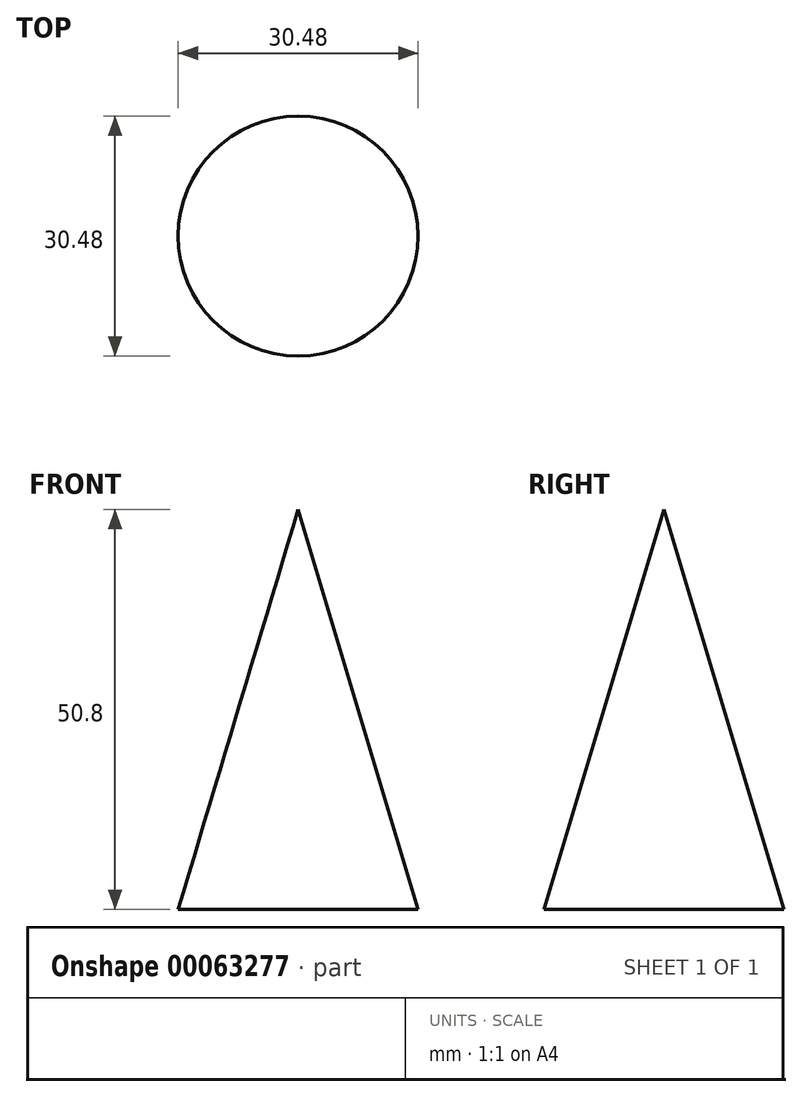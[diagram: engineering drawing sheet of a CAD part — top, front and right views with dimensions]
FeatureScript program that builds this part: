
annotation { "Feature Type Name" : "Feature", "Feature Type Description" : "" }
export const myFeature = defineFeature(function(context is Context, id is Id, definition is map)
    precondition{}
    {
        {
            var Q0;
            Q0=qCreatedBy(makeId("Front.planeOp"),FACE);
            var sketch = newSketch(context, id + "F0", { "sketchPlane" : qUnion([Q0])});
            skLineSegment(sketch, "E0", {"start": v(0, 0) * mm, "end": v(-15.24, 0) * mm});
            skLineSegment(sketch, "E1", {"start": v(-15.24, 0) * mm, "end": v(0, 50.8) * mm});
            skLineSegment(sketch, "E2", {"start": v(0, 50.8) * mm, "end": v(0, 0) * mm});
            skSolve(sketch);
        }
        {
            var Q0;
            Q0 = qSketchRegion(id + "F0", true);
            var Q1;
            Q1=sQuery(id+"F0.wireOp",EDGE,"E2");
            revolve(context, id + "F1", {"entities" : qUnion([Q0]), "axis" : qUnion([Q1]), "revolveType" : RevolveType.FULL});
        }
    });
